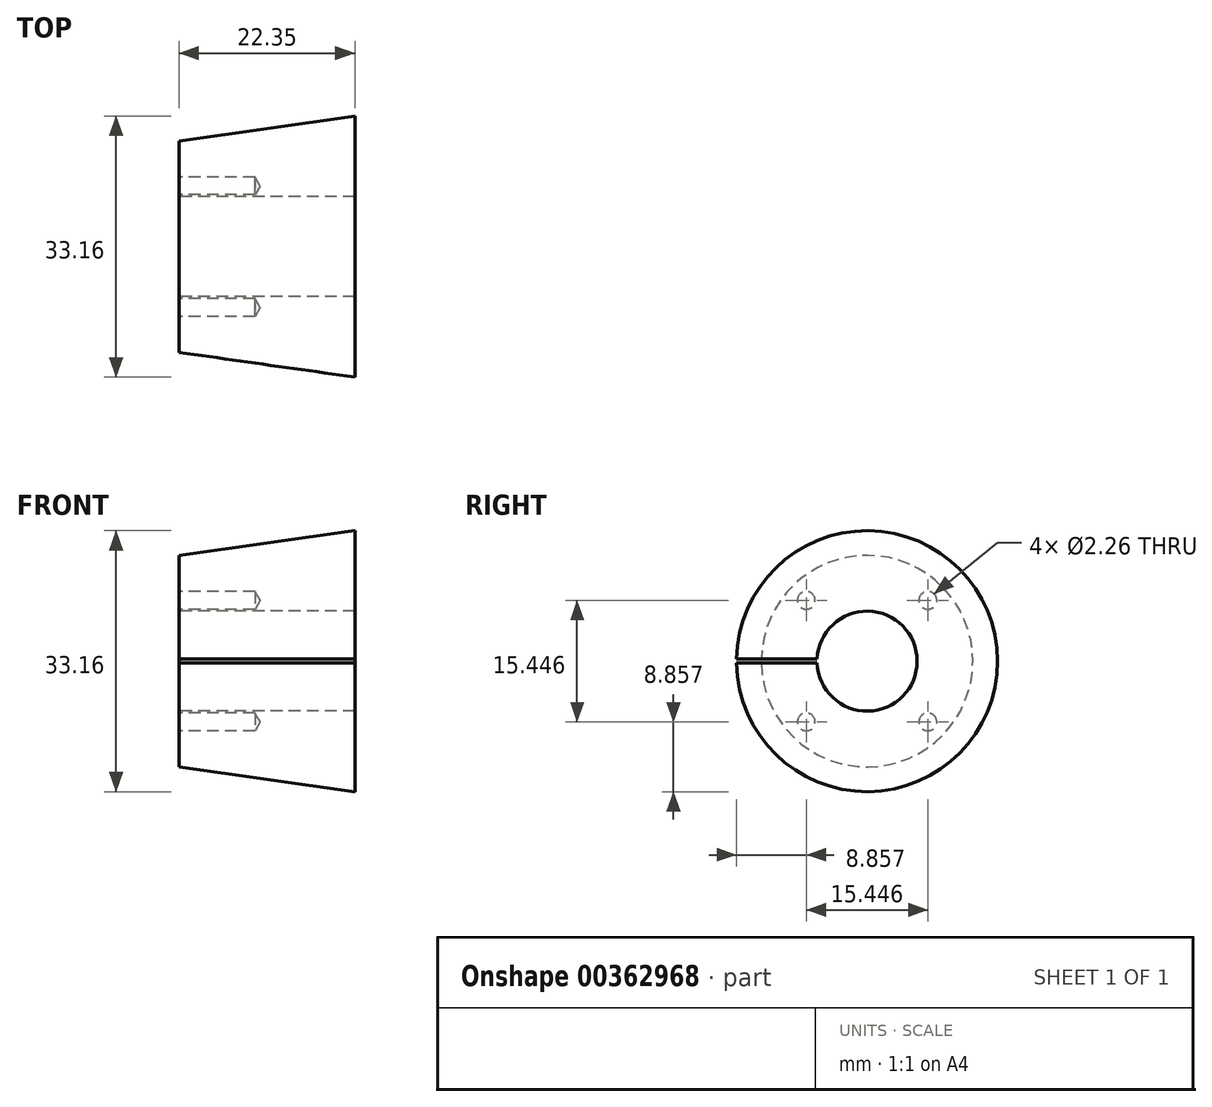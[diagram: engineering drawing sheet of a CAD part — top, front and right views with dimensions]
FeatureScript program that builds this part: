
annotation { "Feature Type Name" : "Feature", "Feature Type Description" : "" }
export const myFeature = defineFeature(function(context is Context, id is Id, definition is map)
    precondition{}
    {
        {
            var Q0;
            Q0=qCreatedBy(makeId("Front.planeOp"),FACE);
            var sketch = newSketch(context, id + "F0", { "sketchPlane" : qUnion([Q0])});
            skLineSegment(sketch, "E0", {"start": v(-41.23, 10.62) * mm, "end": v(-41.23, -16.26) * mm});
            skLineSegment(sketch, "E1", {"start": v(-41.23, -16.26) * mm, "end": v(-18.88, -19.4) * mm});
            skLineSegment(sketch, "E2", {"start": v(-18.88, -19.4) * mm, "end": v(-18.88, 13.76) * mm});
            skLineSegment(sketch, "E3", {"start": v(-18.88, 13.76) * mm, "end": v(-41.23, 10.62) * mm});
            skLineSegment(sketch, "E4", {"start": v(-41.23, -2.82) * mm, "end": v(-18.88, -2.82) * mm, "construction": true});
            skLineSegment(sketch, "E5", {"start": v(-41.23, 3.53) * mm, "end": v(-18.88, 3.53) * mm});
            skSolve(sketch);
        }
        {
            var Q0;
            {var subQ0=sQuery(id+"F0.wireOp",EDGE,"E3");Q0=makeQuery(id+"F0.imprint","IMPRINT",FACE,{"disambiguationData":[TD([[makeQuery(id+"F0.imprint","IMPRINT",EDGE,{"derivedFrom":subQ0}),1.0]])]});}
            var Q1;
            Q1=sQuery(id+"F0.wireOp",EDGE,"E4");
            revolve(context, id + "F1", {"entities" : qUnion([Q0]), "axis" : qUnion([Q1]), "revolveType" : RevolveType.FULL});
        }
        {
            var Q0;
            Q0=makeQuery(id+"F1.opRevolve","SWEPT_FACE",FACE,{"disambiguationData":[OSD([sQuery(id+"F0.wireOp",EDGE,"E0")])]});
            var sketch = newSketch(context, id + "F2", { "sketchPlane" : qUnion([Q0])});
            skPoint(sketch, "E6", {"position": v(0, -2.82) * mm});
            skCircle(sketch, "E7", {"center": v(0, -2.82) * mm, "radius": 10.92 * mm, "construction": true});
            skLineSegment(sketch, "E8", {"start": v(0, -2.82) * mm, "end": v(-12.62, -2.82) * mm, "construction": true});
            skLineSegment(sketch, "E9", {"start": v(0, -2.82) * mm, "end": v(-10.97, 8.15) * mm, "construction": true});
            skPoint(sketch, "E10", {"position": v(-7.72, 4.9) * mm});
            skPoint(sketch, "E11.1.0", {"position": v(-7.72, -10.54) * mm});
            skPoint(sketch, "E11.2.0", {"position": v(7.72, -10.54) * mm});
            skPoint(sketch, "E11.3.0", {"position": v(7.72, 4.9) * mm});
            skLineSegment(sketch, "E12.0", {"start": v(6.34, -2.57) * mm, "end": v(16.58, -2.57) * mm});
            skLineSegment(sketch, "E13.0", {"start": v(6.34, -3.07) * mm, "end": v(16.58, -3.07) * mm});
            skCircle(sketch, "E14.0", {"center": v(0, -2.82) * mm, "radius": 16.58 * mm});
            skCircle(sketch, "E15.0", {"center": v(0, -2.82) * mm, "radius": 6.35 * mm});
            skSolve(sketch);
        }
        {
            var Q0;
            {var subQ0=sQuery(id+"F2.wireOp",EDGE,"E15.0");var subQ1=sQuery(id+"F2.wireOp",EDGE,"E12.0");var subQ2=makeQuery(id+"F2.imprint","INTERSECT",VERTEX,{"derivedFrom":[subQ1,subQ0]});Q0=makeQuery(id+"F2.imprint","IMPRINT",FACE,{"disambiguationData":[TD([[makeQuery(id+"F2.imprint","IMPRINT",EDGE,{"disambiguationData":[TD([[subQ2,1.0]])],"derivedFrom":subQ0}),-1.0]])]});}
            var Q1;
            {var subQ0=sQuery(id+"F2.wireOp",EDGE,"E14.0");var subQ1=sQuery(id+"F2.wireOp",EDGE,"E12.0");var subQ2=makeQuery(id+"F2.imprint","INTERSECT",VERTEX,{"derivedFrom":[subQ1,subQ0]});Q1=makeQuery(id+"F2.imprint","IMPRINT",FACE,{"disambiguationData":[TD([[makeQuery(id+"F2.imprint","IMPRINT",EDGE,{"disambiguationData":[TD([[subQ2,1.0]])],"derivedFrom":subQ0}),1.0]])]});}
            extrude(context, id + "F3", {"entities" : qUnion([Q0, Q1]), "operationType" : NewBodyOperationType.REMOVE, "endBound" : BoundingType.THROUGH_ALL, "oppositeDirection" : true, "depth" : 25.4 * mm});
        }
        {
            var Q0;
            Q0=sQuery(id+"F2.wireOp",VERTEX,"E10");
            var Q1;
            Q1=sQuery(id+"F2.wireOp",VERTEX,"E11.3.0");
            var Q2;
            Q2=sQuery(id+"F2.wireOp",VERTEX,"E11.2.0");
            var Q3;
            Q3=sQuery(id+"F2.wireOp",VERTEX,"E11.1.0");
            var Q4;
            Q4=makeQuery(id+"F1.opRevolve","SWEPT_BODY",BODY,{"disambiguationData":[OSD([sQuery(id+"F0.wireOp",EDGE,"E0"),sQuery(id+"F0.wireOp",EDGE,"E2"),sQuery(id+"F0.wireOp",EDGE,"E3"),sQuery(id+"F0.wireOp",EDGE,"E5")])]});
            hole(context, id + "F4", {"style" : HoleStyle.SIMPLE, "endStyle" : HoleEndStyle.BLIND, "standardTappedOrClearance" : lookupTablePath({ "standard" : "ANSI", "engagement" : "75%", "pitch" : "40 tpi", "size" : "#4", "type" : "Tapped" }), "standardBlindInLast" : lookupTablePath({ "standard" : "ANSI", "engagement" : "75%", "pitch" : "40 tpi", "size" : "#4", "type" : "Tapped" }), "holeDiameter" : 2.26 * mm, "showTappedDepth" : true, "holeDepth" : 9.65 * mm, "tappedDepth" : 7.75 * mm, "tapClearance" : 3, "startFromSketch" : true, "locations" : qUnion([Q0, Q1, Q2, Q3]), "scope" : qUnion([Q4]), "majorDiameter" : 2.84 * mm});
        }
    });
